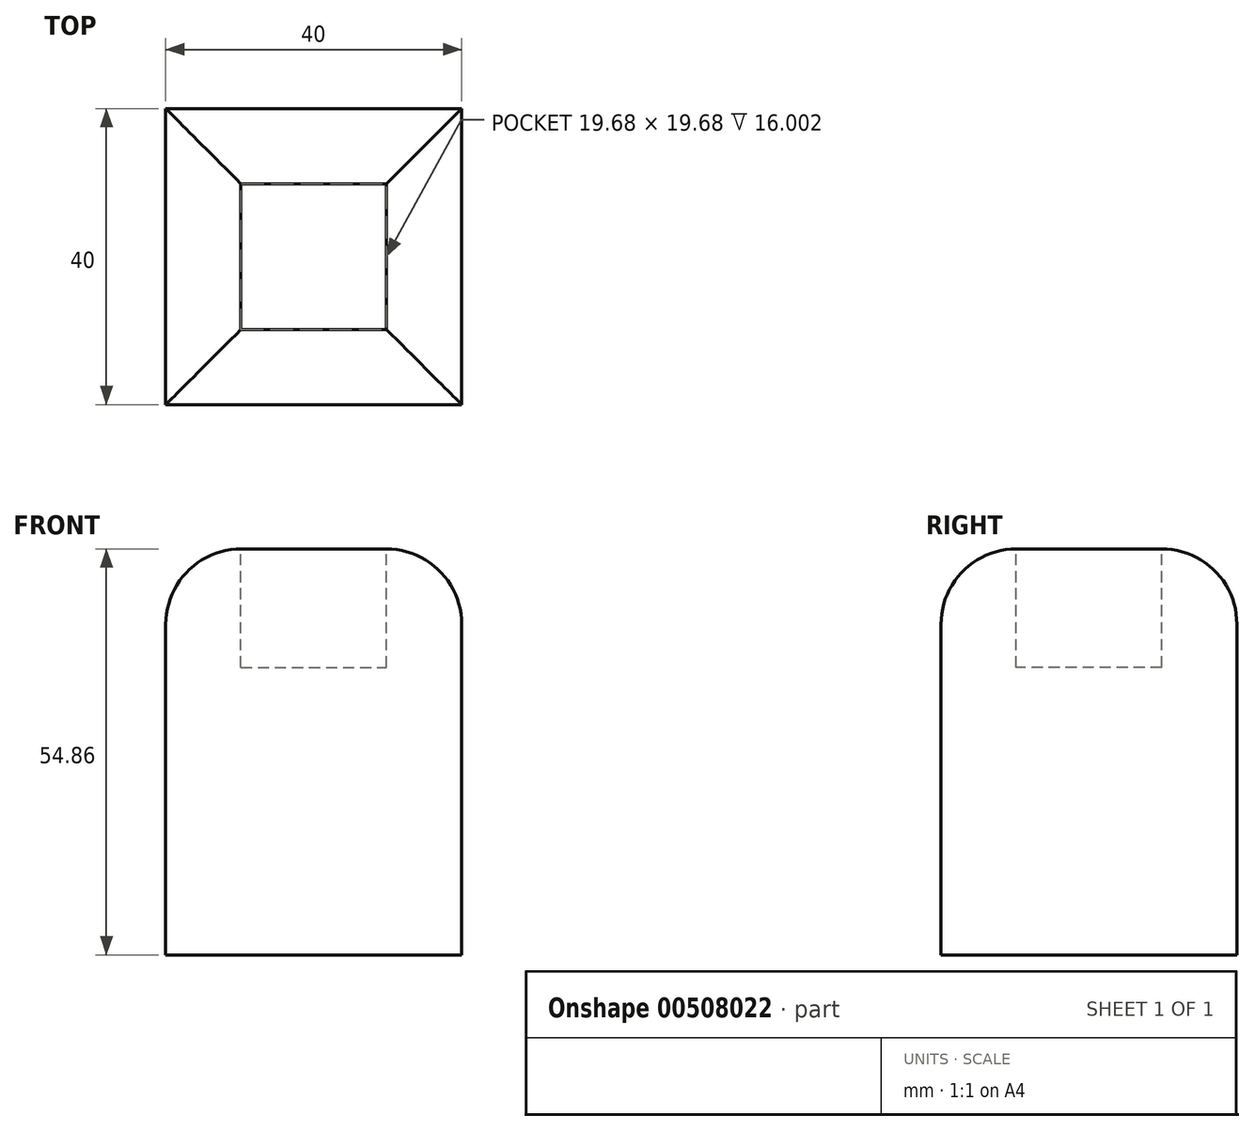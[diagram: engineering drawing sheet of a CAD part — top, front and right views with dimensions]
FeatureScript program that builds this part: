
annotation { "Feature Type Name" : "Feature", "Feature Type Description" : "" }
export const myFeature = defineFeature(function(context is Context, id is Id, definition is map)
    precondition{}
    {
        {
            var Q0;
            Q0=qCreatedBy(makeId("Top.planeOp"),FACE);
            var sketch = newSketch(context, id + "F0", { "sketchPlane" : qUnion([Q0])});
            skLineSegment(sketch, "E0.bottom", {"start": v(-32.08, 16.38) * mm, "end": v(7.92, 16.38) * mm});
            skLineSegment(sketch, "E0.top", {"start": v(-32.08, -23.62) * mm, "end": v(7.92, -23.62) * mm});
            skLineSegment(sketch, "E0.left", {"start": v(-32.08, 16.38) * mm, "end": v(-32.08, -23.62) * mm});
            skLineSegment(sketch, "E0.right", {"start": v(7.92, 16.38) * mm, "end": v(7.92, -23.62) * mm});
            skSolve(sketch);
        }
        {
            var Q0;
            Q0=makeQuery(id+"F0.imprint","IMPRINT",FACE,{"disambiguationData":[TD([[makeQuery(id+"F0.imprint","IMPRINT",EDGE,{"derivedFrom":sQuery(id+"F0.wireOp",EDGE,"E0.bottom")}),-1.0]])]});
            extrude(context, id + "F1", {"entities" : qUnion([Q0]), "depth" : 54.86 * mm});
        }
        {
            var Q0;
            Q0=makeQuery(id+"F1.opExtrude","CAP_EDGE",EDGE,{"disambiguationData":[OSD([sQuery(id+"F0.wireOp",EDGE,"E0.top")])],"isStart":false});
            var Q1;
            Q1=makeQuery(id+"F1.opExtrude","CAP_EDGE",EDGE,{"disambiguationData":[OSD([sQuery(id+"F0.wireOp",EDGE,"E0.right")])],"isStart":false});
            var Q2;
            Q2=makeQuery(id+"F1.opExtrude","CAP_EDGE",EDGE,{"disambiguationData":[OSD([sQuery(id+"F0.wireOp",EDGE,"E0.bottom")])],"isStart":false});
            var Q3;
            Q3=makeQuery(id+"F1.opExtrude","CAP_EDGE",EDGE,{"disambiguationData":[OSD([sQuery(id+"F0.wireOp",EDGE,"E0.left")])],"isStart":false});
            fillet(context, id + "F2", {"entities" : qUnion([Q0, Q1, Q2, Q3]), "radius" : 10.16 * mm, "tangentPropagation" : true, "allowEdgeOverflow" : false});
        }
        {
            var Q0;
            Q0=makeQuery(id+"F1.opExtrude","CAP_FACE",FACE,{"disambiguationData":[OSD([sQuery(id+"F0.wireOp",EDGE,"E0.bottom"),sQuery(id+"F0.wireOp",EDGE,"E0.top"),sQuery(id+"F0.wireOp",EDGE,"E0.left"),sQuery(id+"F0.wireOp",EDGE,"E0.right")])],"isStart":false});
            extrude(context, id + "F3", {"entities" : qUnion([Q0]), "operationType" : NewBodyOperationType.REMOVE, "oppositeDirection" : true, "depth" : 16 * mm});
        }
    });
